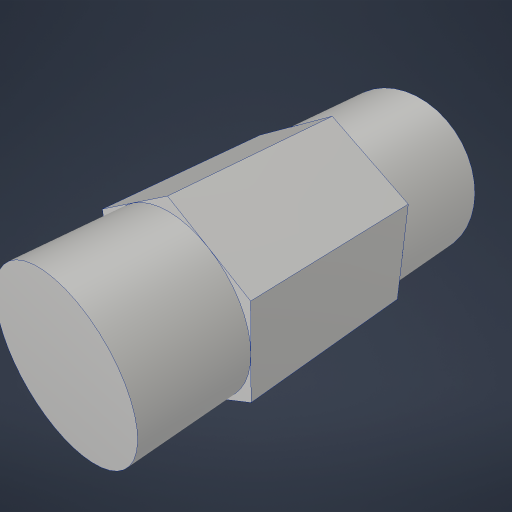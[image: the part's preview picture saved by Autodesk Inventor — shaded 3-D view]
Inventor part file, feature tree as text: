
AUTODESK INVENTOR PART (.ipt)
format: ipt  version: 2023.4 (Build 274418000, 418)  size: 197,120 bytes
history: native  units: in
note: dims shown in document units (in); Inventor stores cm internally (conversion verified against a paired STEP export)
features: extrude x2, mirror x1, projected_geometry x1
ambient origin geometry x8: Origin, YZ Plane, XZ Plane, XY Plane, X Axis, Y Axis, Z Axis, Center Point
bodies: Solid1 (feature_tree)
feature tree (4):
  extrude  "Extrusion1"  TaperAngle=0.0deg  [1 undecoded]
  extrude  "Extrusion2"  TaperAngle=0.0deg  [1 undecoded]
  mirror  "Mirror1"
  projected_geometry  "Projected Loop1"
note: 2 required parameter values undecoded (feature->parameter linkage not recoverable at this tier; creation-order binding heuristic only, values carry confidence <= 0.55)
